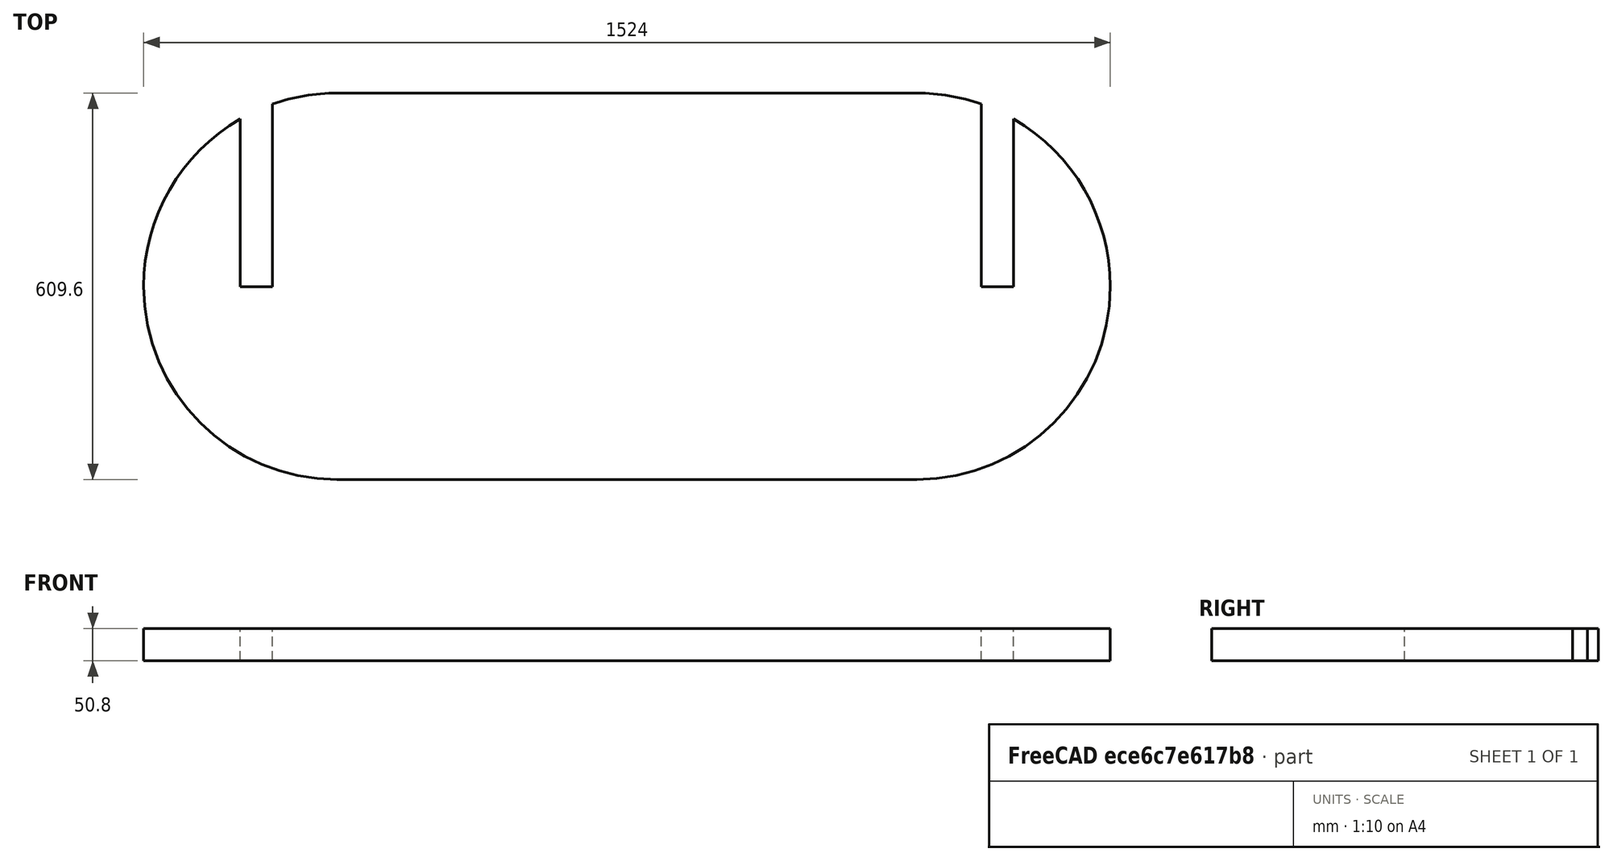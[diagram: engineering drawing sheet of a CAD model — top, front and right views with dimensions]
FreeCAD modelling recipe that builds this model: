
FCSTD DOCUMENT  (FreeCAD 0.21R33771 (Git))
Label: eclipse-2-seat
License: All rights reserved
LicenseURL: http://en.wikipedia.org/wiki/All_rights_reserved
objects: Sketcher::SketchObject×1, PartDesign::Pad×1, PartDesign::Body×1, Spreadsheet::Sheet×1
note: 4 computed .brp shape members not serialized (recipe doc carries the construction recipe); baked Part::Feature solids carry a one-line shape summary decoded from their .brp

FEATURE [Sketcher::SketchObject] Sketch001
  FullyConstrained = false
  MapMode = 5
  Support = -> [XY_Plane001]
  expr: Constraints[14] = <<dims>>.eclipse_height
  expr: Constraints[3] = <<dims>>.eclipse_length
  sketch-geometry (15):
    g0: LineSegment StartX=-1503.82 StartY=-304.048 StartZ=0 EndX=-589.423 EndY=-304.048 EndZ=0
    g1: LineSegment StartX=-589.423 StartY=305.552 StartZ=0 EndX=-1503.82 EndY=305.552 EndZ=0
    g2: GeomPoint X=0 Y=0 Z=0
    g3: ArcOfCircle CenterX=-589.423 CenterY=0.751986 CenterZ=0 NormalX=0 NormalY=0 NormalZ=1 AngleXU=0 Radius=304.8 StartAngle=0 EndAngle=1.0472
    g4: ArcOfCircle CenterX=-589.423 CenterY=0.751986 CenterZ=0 NormalX=0 NormalY=0 NormalZ=1 AngleXU=0 Radius=304.8 StartAngle=4.71239 EndAngle=6.28319
    g5: ArcOfCircle CenterX=-1503.82 CenterY=0.751986 CenterZ=0 NormalX=0 NormalY=0 NormalZ=1 AngleXU=0 Radius=304.8 StartAngle=3.14159 EndAngle=4.71239
    g6: ArcOfCircle CenterX=-1503.82 CenterY=0.751986 CenterZ=0 NormalX=0 NormalY=0 NormalZ=1 AngleXU=0 Radius=304.8 StartAngle=1.5708 EndAngle=1.91063
    g7: LineSegment StartX=-1605.42 StartY=288.12 StartZ=0 EndX=-1605.42 EndY=0 EndZ=0
    g8: LineSegment StartX=-1656.22 StartY=264.717 StartZ=0 EndX=-1656.22 EndY=0 EndZ=0
    g9: LineSegment StartX=-1656.22 StartY=0 StartZ=0 EndX=-1605.42 EndY=0 EndZ=0
    g10: LineSegment StartX=-437.023 StartY=264.716 StartZ=0 EndX=-437.023 EndY=0 EndZ=0
    g11: LineSegment StartX=-487.823 StartY=288.12 StartZ=0 EndX=-487.823 EndY=0 EndZ=0
    g12: LineSegment StartX=-487.823 StartY=0 StartZ=0 EndX=-437.023 EndY=0 EndZ=0
    g13: ArcOfCircle CenterX=-1503.82 CenterY=0.751986 CenterZ=0 NormalX=0 NormalY=0 NormalZ=1 AngleXU=0 Radius=304.8 StartAngle=2.0944 EndAngle=3.14159
    g14: ArcOfCircle CenterX=-589.423 CenterY=0.751986 CenterZ=0 NormalX=0 NormalY=0 NormalZ=1 AngleXU=0 Radius=304.8 StartAngle=1.23096 EndAngle=1.5708
  constraints (37):
    c: Horizontal(g0)
    c: Horizontal(g1)
    c: Coincident(g2,g-1)
    c: DistanceX(g1,g1) = 914.4
    c: Equal(g5,g4)
    c: Coincident(g6,g5)
    c: Coincident(g13,g5)
    c: Coincident(g4,g3)
    c: Coincident(g4,g0)
    c: Coincident(g14,g1)
    c: Coincident(g6,g1)
    c: Coincident(g5,g0)
    c: Equal(g5,g3)
    c: Radius(g6) = 304.8
    c: DistanceY(g0,g1) = 609.6
    c: Horizontal(g3,g3)
    c: Horizontal(g3,g5)
    c: Horizontal(g5,g5)
    c: Vertical(g1,g0)
    c: Vertical(g7)
    c: Vertical(g8)
    c: PointOnObject(g7,g-1)
    c: Coincident(g9,g8)
    c: Coincident(g9,g7)
    c: Vertical(g11)
    c: Vertical(g10)
    c: Coincident(g12,g11)
    c: Coincident(g12,g10)
    c: Horizontal(g12)
    c: Equal(g6,g13)
    c: Coincident(g6,g13)
    c: Coincident(g8,g13)
    c: Coincident(g7,g6)
    c: Equal(g3,g14)
    c: Coincident(g3,g10)
    c: Coincident(g14,g11)
    c: Coincident(g3,g14)
FEATURE [PartDesign::Pad] Pad001
  Direction = (0,0,1)
  Length = 50.8
  Length2 = 10
  Profile = -> Sketch001
  ReferenceAxis = -> Sketch001 [N_Axis]
  Type = 0
  expr: Length = <<dims>>.thickness
FEATURE [PartDesign::Body] Body001
  Group = -> [Sketch001,Pad001]
  Origin = -> Origin001
  Placement = pos=(1654,-190,-24) rot=(0,0,1;0rad)
  Tip = -> Pad001
FEATURE [Spreadsheet::Sheet] Spreadsheet  label="dims"
  cells = B2='eclipse_length; C2(eclipse_length)==36 in; B3='eclipse_height; C3(eclipse_height)==24 in; B4='thickness; C4(thickness)==2 in; B5='slot_from_end; C5(slot_from_end)==6 in; B6='seat_length; C6(seat_length)==48 in
